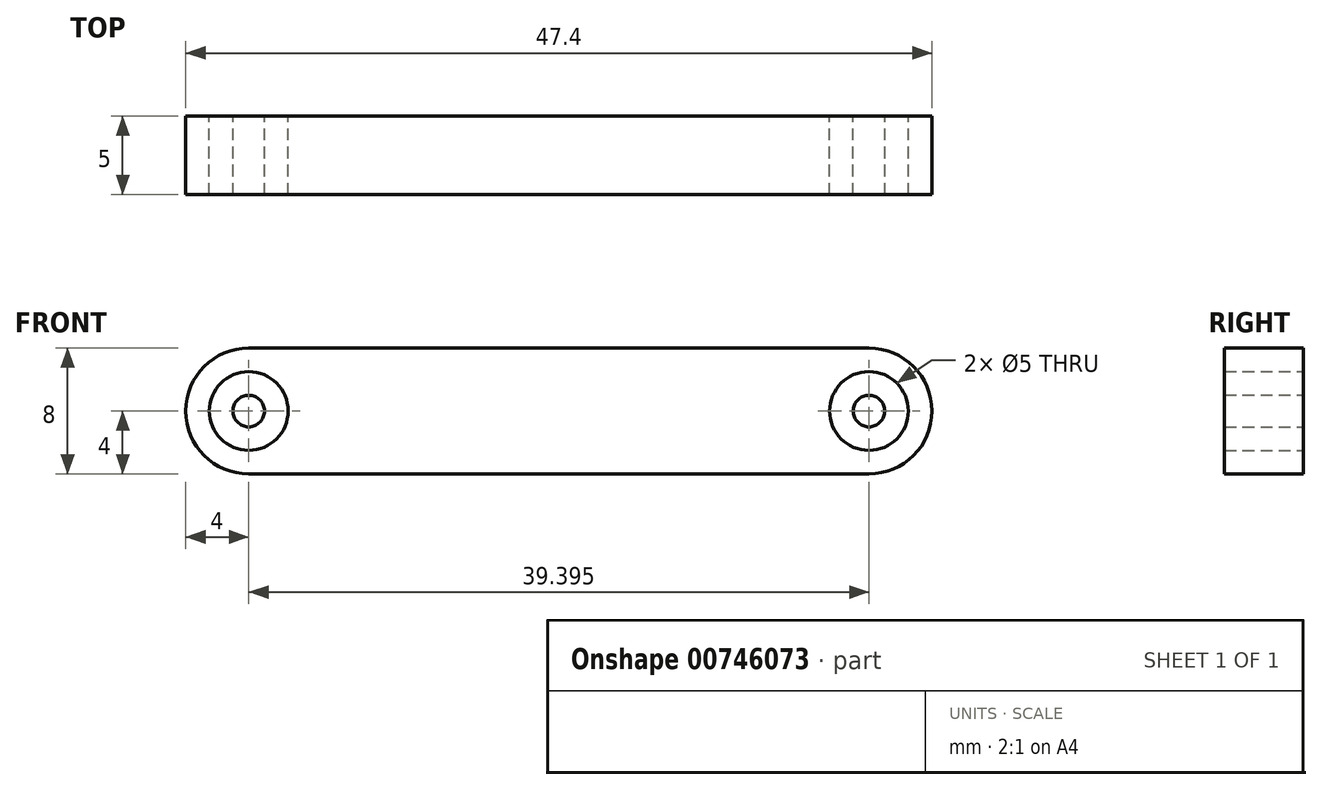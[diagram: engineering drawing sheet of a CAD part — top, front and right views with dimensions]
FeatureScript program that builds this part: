
annotation { "Feature Type Name" : "Feature", "Feature Type Description" : "" }
export const myFeature = defineFeature(function(context is Context, id is Id, definition is map)
    precondition{}
    {
        {
            var Q0;
            Q0=qCreatedBy(makeId("Front.planeOp"),FACE);
            var sketch = newSketch(context, id + "F0", { "sketchPlane" : qUnion([Q0])});
            skArc(sketch, "E0", {"start": v(0, 4) * mm, "mid": v(-4, 0) * mm, "end": v(0, -4) * mm});
            skCircle(sketch, "E1", {"center": v(0, 0) * mm, "radius": 2.5 * mm});
            skCircle(sketch, "E2", {"center": v(0, 0) * mm, "radius": 1 * mm});
            skArc(sketch, "E3", {"start": v(39.4, -4) * mm, "mid": v(43.4, 0) * mm, "end": v(39.4, 4) * mm});
            skCircle(sketch, "E4", {"center": v(39.4, 0) * mm, "radius": 2.5 * mm});
            skCircle(sketch, "E5", {"center": v(39.4, 0) * mm, "radius": 1 * mm});
            skLineSegment(sketch, "E6", {"start": v(0, 4) * mm, "end": v(39.4, 4) * mm});
            skLineSegment(sketch, "E7", {"start": v(0, -4) * mm, "end": v(39.4, -4) * mm});
            skSolve(sketch);
        }
        {
            var Q0;
            Q0=makeQuery(id+"F0.imprint","IMPRINT",FACE,{"disambiguationData":[TD([[makeQuery(id+"F0.imprint","IMPRINT",EDGE,{"derivedFrom":sQuery(id+"F0.wireOp",EDGE,"E0")}),1.0]])]});
            var Q1;
            Q1=makeQuery(id+"F0.imprint","IMPRINT",FACE,{"disambiguationData":[TD([[makeQuery(id+"F0.imprint","IMPRINT",EDGE,{"derivedFrom":sQuery(id+"F0.wireOp",EDGE,"E5")}),1.0]])]});
            var Q2;
            Q2=makeQuery(id+"F0.imprint","IMPRINT",FACE,{"disambiguationData":[TD([[makeQuery(id+"F0.imprint","IMPRINT",EDGE,{"derivedFrom":sQuery(id+"F0.wireOp",EDGE,"E2")}),1.0]])]});
            extrude(context, id + "F1", {"entities" : qUnion([Q0, Q1, Q2]), "depth" : 5 * mm, "offsetDistance" : 25.4 * mm});
        }
    });
